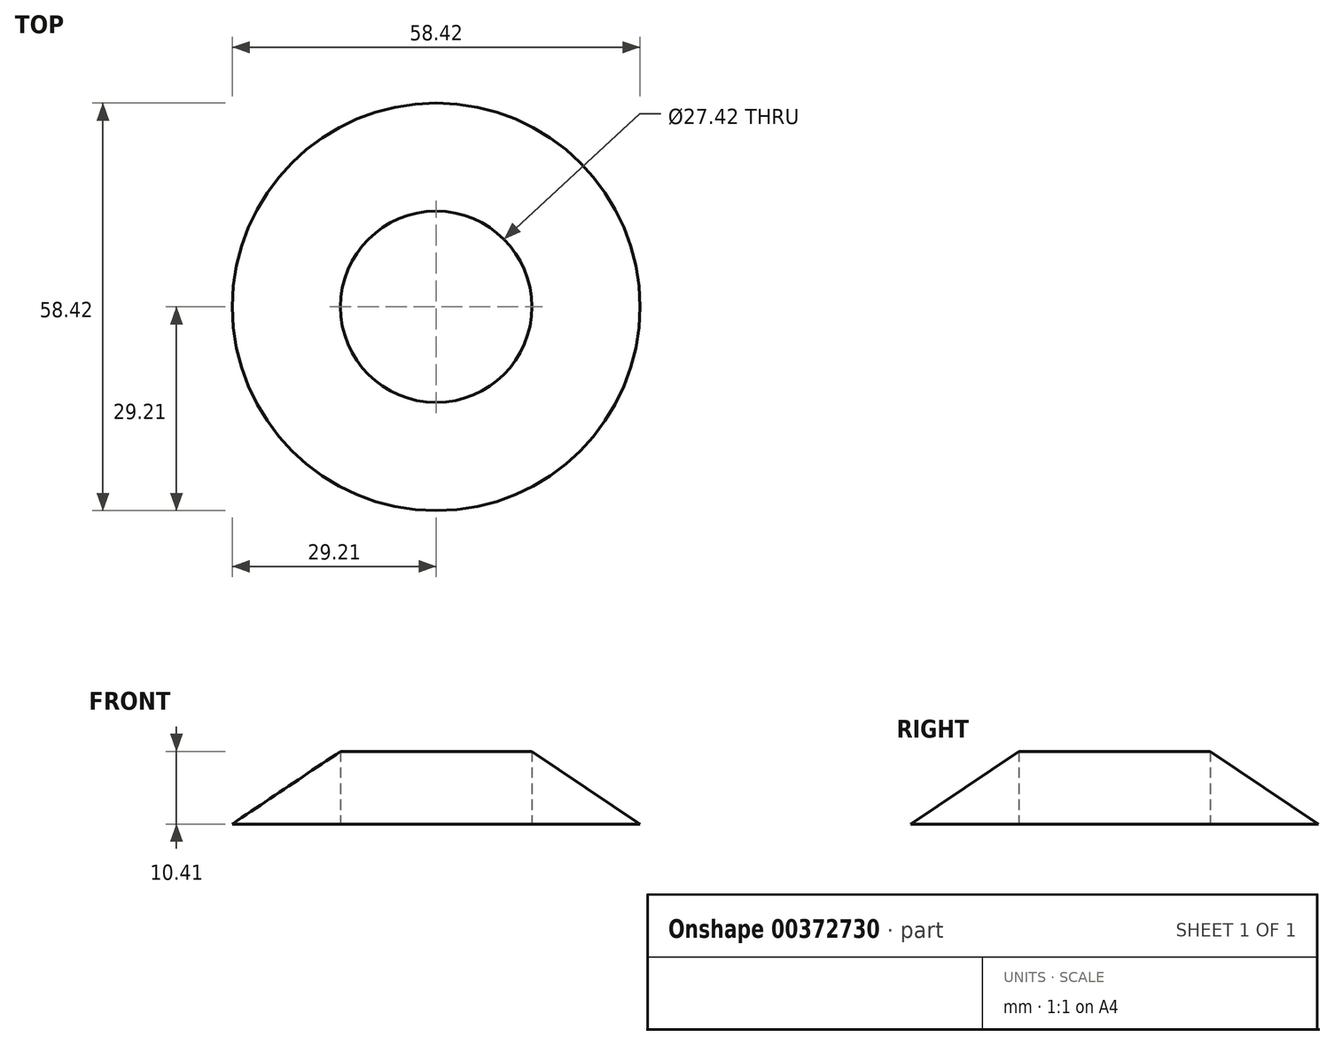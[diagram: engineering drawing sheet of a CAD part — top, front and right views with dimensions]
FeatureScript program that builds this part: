
annotation { "Feature Type Name" : "Feature", "Feature Type Description" : "" }
export const myFeature = defineFeature(function(context is Context, id is Id, definition is map)
    precondition{}
    {
        {
            var Q0;
            Q0=qCreatedBy(makeId("Top.planeOp"),FACE);
            var sketch = newSketch(context, id + "F0", { "sketchPlane" : qUnion([Q0])});
            skCircle(sketch, "E0", {"center": v(0, 0) * mm, "radius": 29.21 * mm});
            skSolve(sketch);
        }
        {
            var Q0;
            Q0=qCreatedBy(makeId("Top.planeOp"),FACE);
            cPlane(context, id + "F1", {"entities" : qUnion([Q0]), "cplaneType" : CPlaneType.OFFSET, "offset" : 10.4 * mm, "width" : 152.4 * mm, "height" : 152.4 * mm});
        }
        {
            var Q0;
            Q0=qCreatedBy(id+"F1.planeOp",FACE);
            var sketch = newSketch(context, id + "F2", { "sketchPlane" : qUnion([Q0])});
            skCircle(sketch, "E1", {"center": v(0, 0) * mm, "radius": 13.71 * mm});
            skSolve(sketch);
        }
        {
            var Q0;
            Q0=makeQuery(id+"F0.imprint","IMPRINT",FACE,{"disambiguationData":[TD([[makeQuery(id+"F0.imprint","IMPRINT",EDGE,{"derivedFrom":sQuery(id+"F0.wireOp",EDGE,"E0")}),1.0]])]});
            var Q1;
            Q1=makeQuery(id+"F2.imprint","IMPRINT",FACE,{"disambiguationData":[TD([[makeQuery(id+"F2.imprint","IMPRINT",EDGE,{"derivedFrom":sQuery(id+"F2.wireOp",EDGE,"E1")}),1.0]])]});
            loft(context, id + "F3", {"sheetProfilesArray" : [{ "sheetProfileEntities" : qUnion([Q0]) }, { "sheetProfileEntities" : qUnion([Q1]) }]});
        }
        {
            var Q0;
            Q0=qCreatedBy(id+"F1.planeOp",FACE);
            var sketch = newSketch(context, id + "F4", { "sketchPlane" : qUnion([Q0])});
            skCircle(sketch, "E2.0", {"center": v(0, 0) * mm, "radius": 13.71 * mm});
            skSolve(sketch);
        }
        {
            var Q0;
            Q0 = qSketchRegion(id + "F4", true);
            var Q1;
            Q1=sQuery(id+"F4.wireOp",EDGE,"E2.0");
            extrude(context, id + "F5", {"entities" : qUnion([Q0]), "bodyType" : ToolBodyType.SURFACE, "surfaceEntities" : qUnion([Q1]), "depth" : 2.54 * mm});
        }
        {
            var Q0;
            Q0=qCreatedBy(makeId("Top.planeOp"),FACE);
            var sketch = newSketch(context, id + "F6", { "sketchPlane" : qUnion([Q0])});
            skCircle(sketch, "E3.0", {"center": v(0, 0) * mm, "radius": 13.71 * mm});
            skSolve(sketch);
        }
        {
            var Q0;
            Q0 = qSketchRegion(id + "F6", true);
            extrude(context, id + "F7", {"entities" : qUnion([Q0]), "operationType" : NewBodyOperationType.REMOVE, "depth" : 37.85 * mm});
        }
    });
